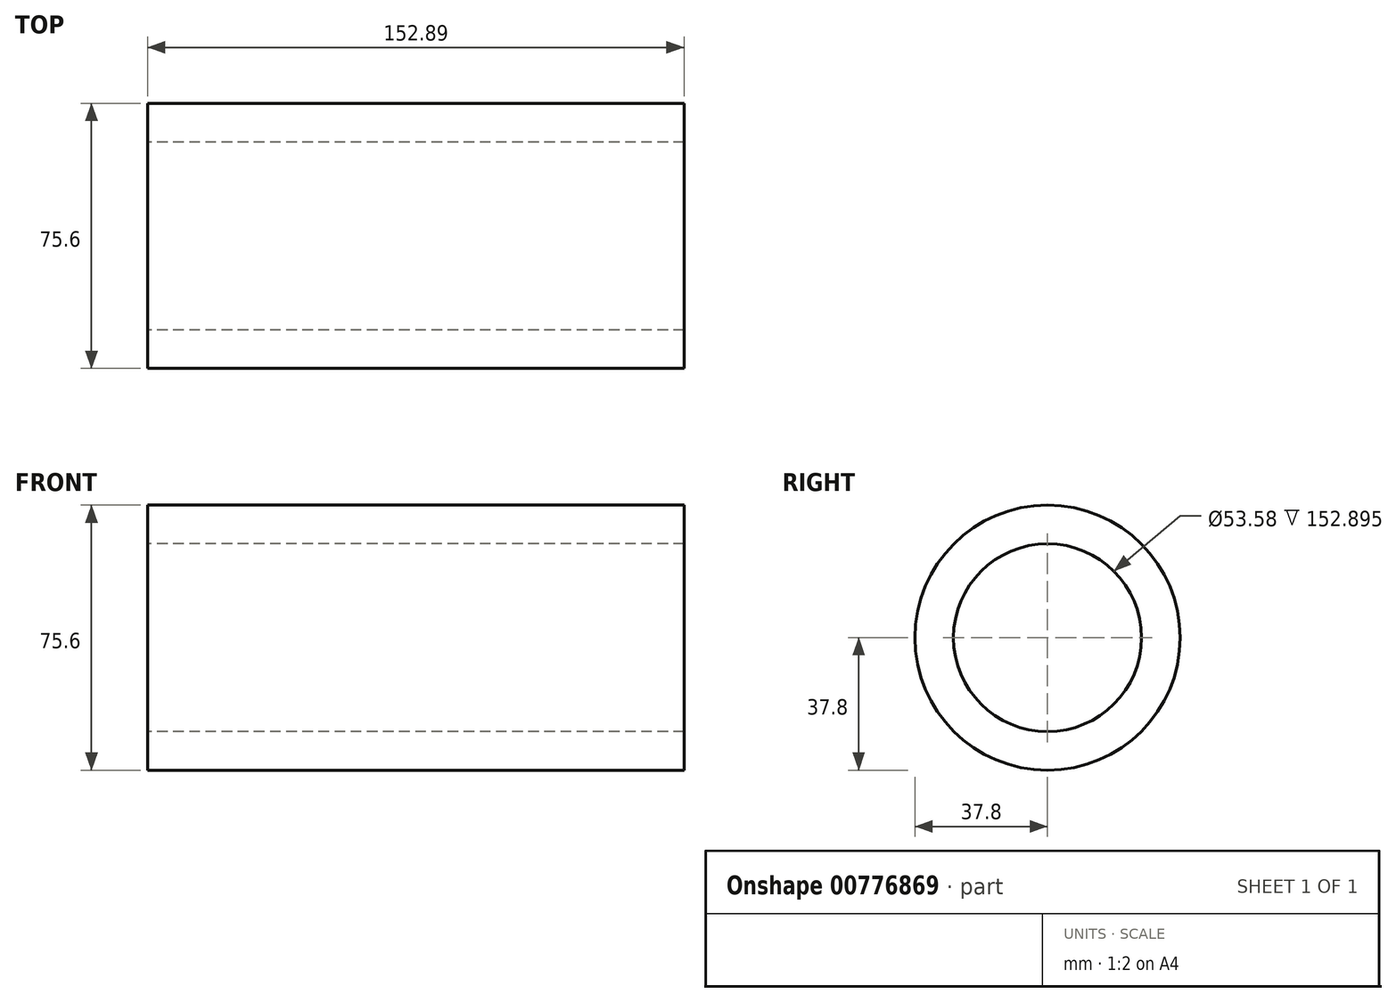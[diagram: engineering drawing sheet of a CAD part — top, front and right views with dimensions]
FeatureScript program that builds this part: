
annotation { "Feature Type Name" : "Feature", "Feature Type Description" : "" }
export const myFeature = defineFeature(function(context is Context, id is Id, definition is map)
    precondition{}
    {
        {
            var Q0;
            Q0=qCreatedBy(makeId("Front.planeOp"),FACE);
            var sketch = newSketch(context, id + "F0", { "sketchPlane" : qUnion([Q0])});
            skLineSegment(sketch, "E0", {"start": v(0, 0) * mm, "end": v(-90.53, 0) * mm, "construction": true});
            skLineSegment(sketch, "E1", {"start": v(0, 0) * mm, "end": v(92.24, 0) * mm, "construction": true});
            skLineSegment(sketch, "E2.bottom", {"start": v(8.8, 43.92) * mm, "end": v(27.4, 43.92) * mm, "construction": true});
            skLineSegment(sketch, "E2.top", {"start": v(8.8, 33.64) * mm, "end": v(27.4, 33.64) * mm, "construction": true});
            skLineSegment(sketch, "E2.left", {"start": v(8.8, 43.92) * mm, "end": v(8.8, 33.64) * mm, "construction": true});
            skLineSegment(sketch, "E2.right", {"start": v(27.4, 43.92) * mm, "end": v(27.4, 33.64) * mm, "construction": true});
            skSolve(sketch);
        }
        {
            var Q0;
            Q0=qCreatedBy(makeId("Front.planeOp"),FACE);
            var sketch = newSketch(context, id + "F1", { "sketchPlane" : qUnion([Q0])});
            skLineSegment(sketch, "E3", {"start": v(0, 0) * mm, "end": v(-101.79, 0) * mm});
            skLineSegment(sketch, "E4", {"start": v(0, 0) * mm, "end": v(88.57, 0) * mm});
            skLineSegment(sketch, "E5.bottom", {"start": v(4.9, 37.8) * mm, "end": v(22.51, 37.8) * mm});
            skLineSegment(sketch, "E5.top", {"start": v(4.9, 26.8) * mm, "end": v(22.51, 26.8) * mm});
            skLineSegment(sketch, "E5.left", {"start": v(4.9, 37.8) * mm, "end": v(4.9, 26.8) * mm});
            skLineSegment(sketch, "E5.right", {"start": v(22.51, 37.8) * mm, "end": v(22.51, 26.8) * mm});
            skLineSegment(sketch, "E6.bottom", {"start": v(-128.21, 23.86) * mm, "end": v(-108.64, 23.86) * mm});
            skLineSegment(sketch, "E6.top", {"start": v(-128.21, 26.8) * mm, "end": v(-108.64, 26.8) * mm});
            skLineSegment(sketch, "E6.left", {"start": v(-128.21, 23.86) * mm, "end": v(-128.21, 26.8) * mm});
            skLineSegment(sketch, "E6.right", {"start": v(-108.64, 23.86) * mm, "end": v(-108.64, 26.8) * mm});
            skSolve(sketch);
        }
        {
            var Q0;
            Q0=makeQuery(id+"F1.imprint","IMPRINT",FACE,{"disambiguationData":[TD([[makeQuery(id+"F1.imprint","IMPRINT",EDGE,{"derivedFrom":sQuery(id+"F1.wireOp",EDGE,"E5.bottom")}),-1.0]])]});
            var Q1;
            Q1=sQuery(id+"F1.wireOp",EDGE,"E4");
            revolve(context, id + "F2", {"surfaceOperationType" : NewSurfaceOperationType.NEW, "entities" : qUnion([Q0]), "axis" : qUnion([Q1]), "revolveType" : RevolveType.FULL});
        }
        {
            var Q0;
            Q0=qCreatedBy(makeId("Right.planeOp"),FACE);
            var sketch = newSketch(context, id + "F3", { "sketchPlane" : qUnion([Q0])});
            skCircle(sketch, "E7", {"center": v(0, 33.15) * mm, "radius": 2.64 * mm});
            skCircle(sketch, "E8.1.0", {"center": v(-11.34, 31.15) * mm, "radius": 2.64 * mm});
            skCircle(sketch, "E8.2.0", {"center": v(-21.31, 25.4) * mm, "radius": 2.64 * mm});
            skCircle(sketch, "E8.3.0", {"center": v(-28.71, 16.58) * mm, "radius": 2.64 * mm});
            skCircle(sketch, "E8.4.0", {"center": v(-32.65, 5.76) * mm, "radius": 2.64 * mm});
            skCircle(sketch, "E8.5.0", {"center": v(-32.65, -5.76) * mm, "radius": 2.64 * mm});
            skCircle(sketch, "E8.6.0", {"center": v(-28.71, -16.58) * mm, "radius": 2.64 * mm});
            skCircle(sketch, "E8.7.0", {"center": v(-21.31, -25.4) * mm, "radius": 2.64 * mm});
            skCircle(sketch, "E8.8.0", {"center": v(-11.34, -31.15) * mm, "radius": 2.64 * mm});
            skCircle(sketch, "E8.9.0", {"center": v(0, -33.15) * mm, "radius": 2.64 * mm});
            skCircle(sketch, "E8.10.0", {"center": v(11.34, -31.15) * mm, "radius": 2.64 * mm});
            skCircle(sketch, "E8.11.0", {"center": v(21.31, -25.4) * mm, "radius": 2.64 * mm});
            skPoint(sketch, "E8.center", {"position": v(0, 0) * mm});
            skCircle(sketch, "E9.1.12.0", {"center": v(28.71, -16.58) * mm, "radius": 2.64 * mm});
            skCircle(sketch, "E9.1.13.0", {"center": v(32.65, -5.76) * mm, "radius": 2.64 * mm});
            skCircle(sketch, "E9.1.14.0", {"center": v(32.65, 5.76) * mm, "radius": 2.64 * mm});
            skCircle(sketch, "E10.1.15.0", {"center": v(28.71, 16.58) * mm, "radius": 2.64 * mm});
            skCircle(sketch, "E10.1.16.0", {"center": v(21.31, 25.4) * mm, "radius": 2.64 * mm});
            skCircle(sketch, "E10.1.17.0", {"center": v(11.34, 31.15) * mm, "radius": 2.64 * mm});
            skSolve(sketch);
        }
        {
            var Q0;
            Q0=sQuery(id+"F3.wireOp",EDGE,"E7");
            extrude(context, id + "F4", {"bodyType" : ToolBodyType.SURFACE, "surfaceEntities" : qUnion([Q0]), "endBound" : BoundingType.THROUGH_ALL, "depth" : 25.4 * mm, "offsetDistance" : 25.4 * mm});
        }
        {
            var Q0;
            Q0=makeQuery(id+"F2.opRevolve","SWEPT_FACE",FACE,{"disambiguationData":[OSD([sQuery(id+"F1.wireOp",EDGE,"E5.right")])]});
            var sketch = newSketch(context, id + "F5", { "sketchPlane" : qUnion([Q0])});
            skSolve(sketch);
        }
        {
            var Q0;
            {var subQ0=sQuery(id+"F1.wireOp",EDGE,"E5.right");Q0=makeQuery(id+"F5.imprint","IMPRINT",FACE,{"disambiguationData":[TD([[makeQuery(id+"F5.imprint","IMPRINT",EDGE,{"derivedFrom":makeQuery(id+"F2.opRevolve","SWEPT_EDGE",EDGE,{"disambiguationData":[OSD([sQuery(id+"F1.wireOp",EDGE,"E5.bottom"),subQ0])]})}),-1.0]])]});}
            extrude(context, id + "F6", {"entities" : qUnion([Q0]), "operationType" : NewBodyOperationType.ADD, "endBound" : BoundingType.THROUGH_ALL, "oppositeDirection" : true, "depth" : 25.4 * mm, "offsetDistance" : 25.4 * mm});
        }
    });
